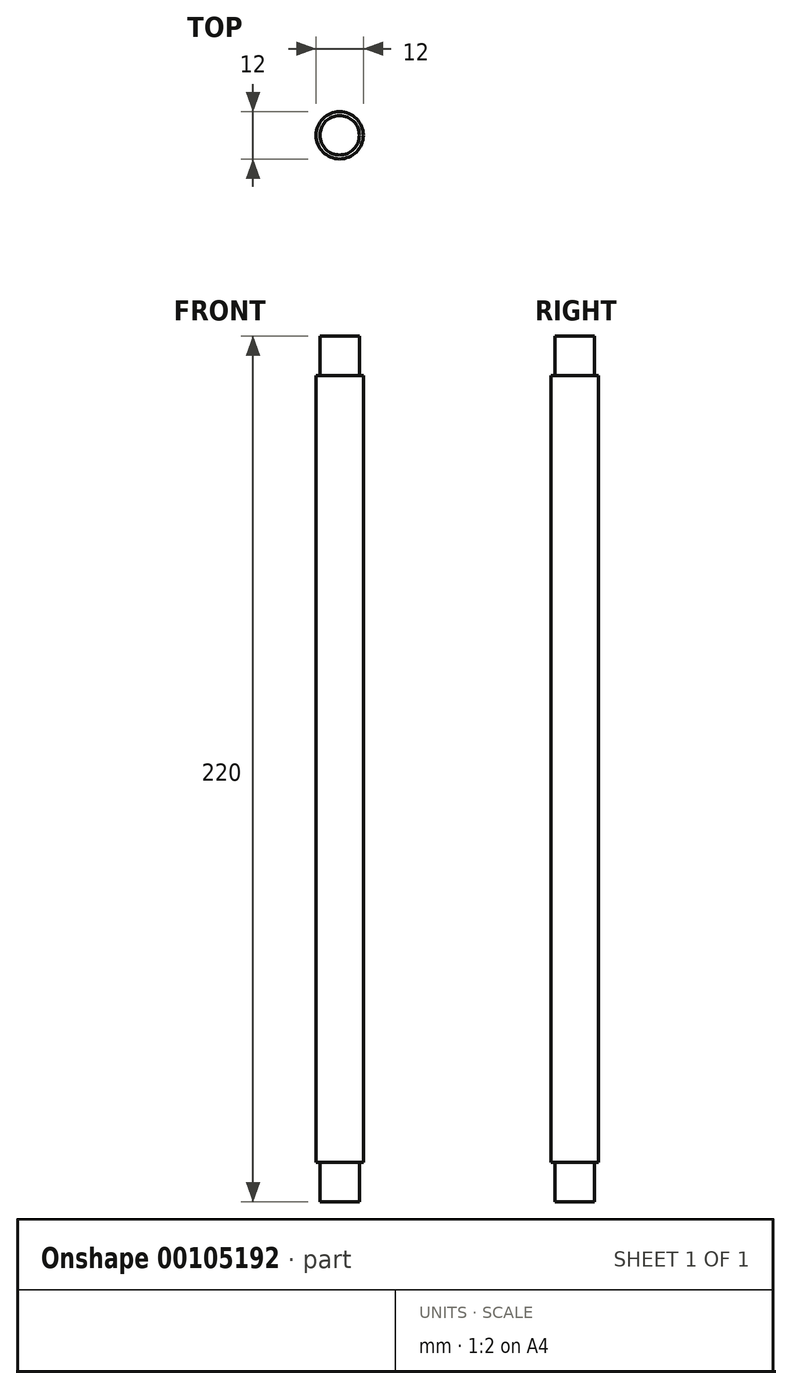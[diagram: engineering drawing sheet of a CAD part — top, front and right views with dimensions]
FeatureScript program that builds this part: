
annotation { "Feature Type Name" : "Feature", "Feature Type Description" : "" }
export const myFeature = defineFeature(function(context is Context, id is Id, definition is map)
    precondition{}
    {
        {
            var Q0;
            Q0=qCreatedBy(makeId("Top.planeOp"),FACE);
            var sketch = newSketch(context, id + "F0", { "sketchPlane" : qUnion([Q0])});
            skCircle(sketch, "E0", {"center": v(0, 0) * mm, "radius": 6 * mm});
            skSolve(sketch);
        }
        {
            var Q0;
            Q0 = qSketchRegion(id + "F0", true);
            extrude(context, id + "F1", {"entities" : qUnion([Q0]), "depth" : 200 * mm});
        }
        {
            var Q0;
            Q0=makeQuery(id+"F1.opExtrude","CAP_FACE",FACE,{"disambiguationData":[OSD([sQuery(id+"F0.wireOp",EDGE,"E0")])],"isStart":false});
            var sketch = newSketch(context, id + "F2", { "sketchPlane" : qUnion([Q0])});
            skSolve(sketch);
        }
        {
            var Q0;
            Q0=makeQuery(id+"F2.imprint","IMPRINT",FACE,{"disambiguationData":[TD([[makeQuery(id+"F2.imprint","IMPRINT",EDGE,{"derivedFrom":makeQuery(id+"F1.opExtrude","CAP_EDGE",EDGE,{"disambiguationData":[OSD([sQuery(id+"F0.wireOp",EDGE,"E0")])],"isStart":false})}),1.0]])]});
            var sketch = newSketch(context, id + "F3", { "sketchPlane" : qUnion([Q0])});
            skCircle(sketch, "E1", {"center": v(0, 0) * mm, "radius": 5 * mm});
            skSolve(sketch);
        }
        {
            var Q0;
            Q0 = qSketchRegion(id + "F3", true);
            extrude(context, id + "F4", {"entities" : qUnion([Q0]), "operationType" : NewBodyOperationType.ADD, "depth" : 10 * mm});
        }
        {
            var Q0;
            Q0 = qSketchRegion(id + "F3", true);
            extrude(context, id + "F5", {"entities" : qUnion([Q0]), "operationType" : NewBodyOperationType.ADD, "oppositeDirection" : true, "depth" : 210 * mm});
        }
    });
